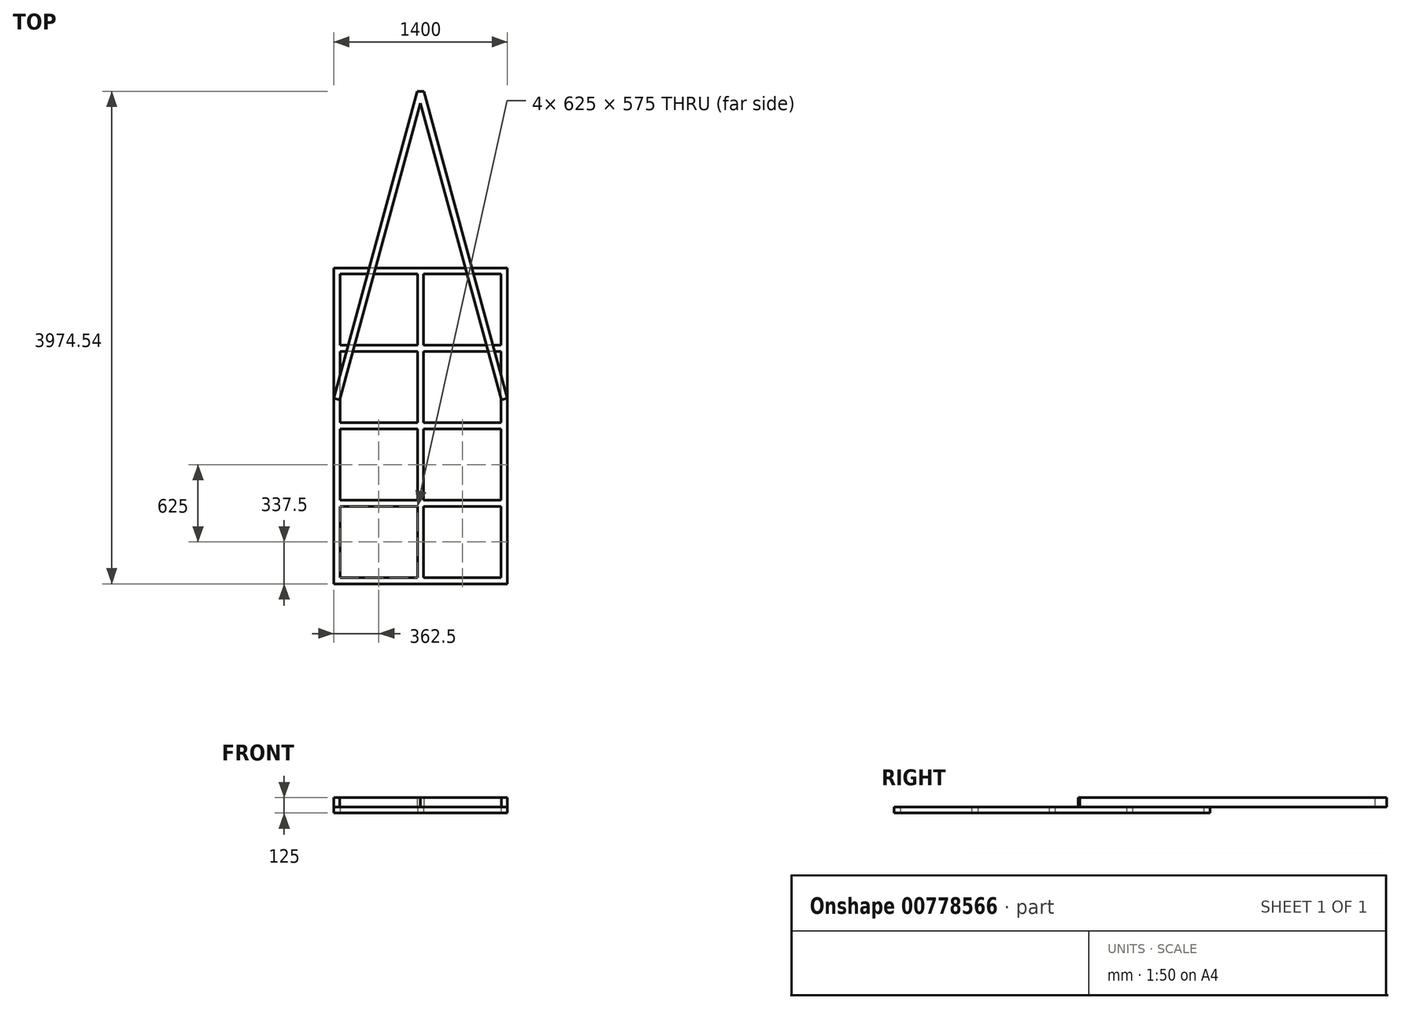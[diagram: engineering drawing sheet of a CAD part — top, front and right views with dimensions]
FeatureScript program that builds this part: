
annotation { "Feature Type Name" : "Feature", "Feature Type Description" : "" }
export const myFeature = defineFeature(function(context is Context, id is Id, definition is map)
    precondition{}
    {
        {
            var Q0;
            Q0=qCreatedBy(makeId("Top.planeOp"),FACE);
            var sketch = newSketch(context, id + "F0", { "sketchPlane" : qUnion([Q0])});
            skLineSegment(sketch, "E0.bottom", {"start": v(700, -1275) * mm, "end": v(-700, -1275) * mm});
            skLineSegment(sketch, "E0.top", {"start": v(700, 1275) * mm, "end": v(-700, 1275) * mm});
            skLineSegment(sketch, "E0.left", {"start": v(700, -1275) * mm, "end": v(700, 1275) * mm});
            skLineSegment(sketch, "E0.right", {"start": v(-700, -1275) * mm, "end": v(-700, 1275) * mm});
            skLineSegment(sketch, "E1", {"start": v(-700, -1275) * mm, "end": v(700, 1275) * mm, "construction": true});
            skLineSegment(sketch, "E2.bottom", {"start": v(-25, 25) * mm, "end": v(-650, 25) * mm});
            skLineSegment(sketch, "E2.top", {"start": v(-25, 1225) * mm, "end": v(-650, 1225) * mm});
            skLineSegment(sketch, "E2.left", {"start": v(-25, 25) * mm, "end": v(-25, 600) * mm});
            skLineSegment(sketch, "E2.right", {"start": v(-650, 25) * mm, "end": v(-650, 600) * mm});
            skPoint(sketch, "E2.middle", {"position": v(-337.5, 625) * mm});
            skLineSegment(sketch, "E3.bottom", {"start": v(650, 25) * mm, "end": v(25, 25) * mm});
            skLineSegment(sketch, "E3.top", {"start": v(650, 1225) * mm, "end": v(25, 1225) * mm});
            skLineSegment(sketch, "E3.left", {"start": v(650, 25) * mm, "end": v(650, 600) * mm});
            skLineSegment(sketch, "E3.right", {"start": v(25, 25) * mm, "end": v(25, 600) * mm});
            skPoint(sketch, "E3.middle", {"position": v(337.5, 625) * mm});
            skLineSegment(sketch, "E4.bottom", {"start": v(650, -1225) * mm, "end": v(25, -1225) * mm});
            skLineSegment(sketch, "E4.top", {"start": v(650, -25) * mm, "end": v(25, -25) * mm});
            skLineSegment(sketch, "E4.left", {"start": v(650, -1225) * mm, "end": v(650, -650) * mm});
            skLineSegment(sketch, "E4.right", {"start": v(25, -1225) * mm, "end": v(25, -650) * mm});
            skPoint(sketch, "E4.middle", {"position": v(337.5, -625) * mm});
            skLineSegment(sketch, "E5.bottom", {"start": v(-25, -1225) * mm, "end": v(-650, -1225) * mm});
            skLineSegment(sketch, "E5.top", {"start": v(-25, -25) * mm, "end": v(-650, -25) * mm});
            skLineSegment(sketch, "E5.left", {"start": v(-25, -1225) * mm, "end": v(-25, -650) * mm});
            skLineSegment(sketch, "E5.right", {"start": v(-650, -1225) * mm, "end": v(-650, -650) * mm});
            skPoint(sketch, "E5.middle", {"position": v(-337.5, -625) * mm});
            skLineSegment(sketch, "E6", {"start": v(0, 1275) * mm, "end": v(0, -1275) * mm, "construction": true});
            skLineSegment(sketch, "E7", {"start": v(-700, 0) * mm, "end": v(700, 0) * mm, "construction": true});
            skLineSegment(sketch, "E8", {"start": v(-650, -625) * mm, "end": v(650, -625) * mm, "construction": true});
            skLineSegment(sketch, "E9", {"start": v(-650, 625) * mm, "end": v(650, 625) * mm, "construction": true});
            skLineSegment(sketch, "E10.bottom", {"start": v(650, 650) * mm, "end": v(25, 650) * mm});
            skLineSegment(sketch, "E10.top", {"start": v(650, 600) * mm, "end": v(25, 600) * mm});
            skPoint(sketch, "E10.middle", {"position": v(0, 625) * mm});
            skLineSegment(sketch, "E11.bottom", {"start": v(650, -600) * mm, "end": v(25, -600) * mm});
            skLineSegment(sketch, "E11.top", {"start": v(650, -650) * mm, "end": v(25, -650) * mm});
            skPoint(sketch, "E11.middle", {"position": v(0, -625) * mm});
            skLineSegment(sketch, "E12.trimOffspring", {"start": v(-650, 650) * mm, "end": v(-650, 1225) * mm});
            skLineSegment(sketch, "E13.trimOffspring", {"start": v(650, 650) * mm, "end": v(650, 1225) * mm});
            skLineSegment(sketch, "E14.trimOffspring", {"start": v(650, -600) * mm, "end": v(650, -25) * mm});
            skLineSegment(sketch, "E15.trimOffspring", {"start": v(-25, -600) * mm, "end": v(-25, -25) * mm});
            skLineSegment(sketch, "E16.trimOffspring", {"start": v(-25, -650) * mm, "end": v(-650, -650) * mm});
            skLineSegment(sketch, "E17.trimOffspring", {"start": v(-25, -600) * mm, "end": v(-650, -600) * mm});
            skLineSegment(sketch, "E18.trimOffspring", {"start": v(25, -600) * mm, "end": v(25, -25) * mm});
            skLineSegment(sketch, "E19.trimOffspring", {"start": v(-25, 650) * mm, "end": v(-25, 1225) * mm});
            skLineSegment(sketch, "E20.trimOffspring", {"start": v(-25, 600) * mm, "end": v(-650, 600) * mm});
            skLineSegment(sketch, "E21.trimOffspring", {"start": v(25, 650) * mm, "end": v(25, 1225) * mm});
            skLineSegment(sketch, "E22.trimOffspring", {"start": v(-25, 650) * mm, "end": v(-650, 650) * mm});
            skLineSegment(sketch, "E23.trimOffspring", {"start": v(-650, -600) * mm, "end": v(-650, -25) * mm});
            skSolve(sketch);
        }
        {
            var Q0;
            Q0 = qSketchRegion(id + "F0", true);
            extrude(context, id + "F1", {"entities" : qUnion([Q0]), "depth" : 50 * mm, "offsetDistance" : 25 * mm});
        }
        {
            var Q0;
            Q0=makeQuery(id+"F1.opExtrude","CAP_FACE",FACE,{"disambiguationData":[OSD([sQuery(id+"F0.wireOp",EDGE,"E0.bottom"),sQuery(id+"F0.wireOp",EDGE,"E0.top"),sQuery(id+"F0.wireOp",EDGE,"E0.left"),sQuery(id+"F0.wireOp",EDGE,"E0.right"),sQuery(id+"F0.wireOp",EDGE,"E2.bottom"),sQuery(id+"F0.wireOp",EDGE,"E2.top"),sQuery(id+"F0.wireOp",EDGE,"E2.left"),sQuery(id+"F0.wireOp",EDGE,"E2.right"),sQuery(id+"F0.wireOp",EDGE,"E3.bottom"),sQuery(id+"F0.wireOp",EDGE,"E3.top"),sQuery(id+"F0.wireOp",EDGE,"E3.left"),sQuery(id+"F0.wireOp",EDGE,"E3.right"),sQuery(id+"F0.wireOp",EDGE,"E4.bottom"),sQuery(id+"F0.wireOp",EDGE,"E4.top"),sQuery(id+"F0.wireOp",EDGE,"E4.left"),sQuery(id+"F0.wireOp",EDGE,"E4.right"),sQuery(id+"F0.wireOp",EDGE,"E5.bottom"),sQuery(id+"F0.wireOp",EDGE,"E5.top"),sQuery(id+"F0.wireOp",EDGE,"E5.left"),sQuery(id+"F0.wireOp",EDGE,"E5.right")])],"isStart":false});
            var sketch = newSketch(context, id + "F2", { "sketchPlane" : qUnion([Q0])});
            skLineSegment(sketch, "E24", {"start": v(0, 0) * mm, "end": v(0, 2700) * mm, "construction": true});
            skLineSegment(sketch, "E25", {"start": v(0, 2700) * mm, "end": v(-650, 312.5) * mm, "construction": true});
            skLineSegment(sketch, "E26", {"start": v(650, 312.5) * mm, "end": v(0, 2700) * mm, "construction": true});
            skLineSegment(sketch, "E27.bottom", {"start": v(-700, 224.02) * mm, "end": v(-651.76, 210.88) * mm});
            skLineSegment(sketch, "E27.left", {"start": v(-700, 224.02) * mm, "end": v(-26.04, 2699.54) * mm});
            skLineSegment(sketch, "E27.right", {"start": v(-651.76, 210.88) * mm, "end": v(0, 2604.83) * mm});
            skPoint(sketch, "E27.middle", {"position": v(-325, 1506.25) * mm});
            skLineSegment(sketch, "E28.bottom", {"start": v(700, 224.02) * mm, "end": v(651.76, 210.88) * mm});
            skLineSegment(sketch, "E28.left", {"start": v(700, 224.02) * mm, "end": v(26.04, 2699.54) * mm});
            skLineSegment(sketch, "E28.right", {"start": v(651.76, 210.88) * mm, "end": v(0, 2604.83) * mm});
            skPoint(sketch, "E28.middle", {"position": v(325, 1506.25) * mm});
            skLineSegment(sketch, "E29", {"start": v(26.04, 2699.54) * mm, "end": v(-26.04, 2699.54) * mm});
            skPoint(sketch, "E28.top.end.orphan", {"position": v(-50, 2788.48) * mm});
            skPoint(sketch, "E30.orphan", {"position": v(50, 2788.48) * mm});
            skPoint(sketch, "E31.trimOffspring.end.orphan", {"position": v(-1.76, 2801.62) * mm});
            skPoint(sketch, "E32.trimOffspring.end.orphan", {"position": v(1.76, 2801.62) * mm});
            skSolve(sketch);
        }
        {
            var Q0;
            Q0 = qSketchRegion(id + "F2", true);
            extrude(context, id + "F3", {"entities" : qUnion([Q0]), "operationType" : NewBodyOperationType.ADD, "depth" : 75 * mm, "offsetDistance" : 25 * mm});
        }
    });
